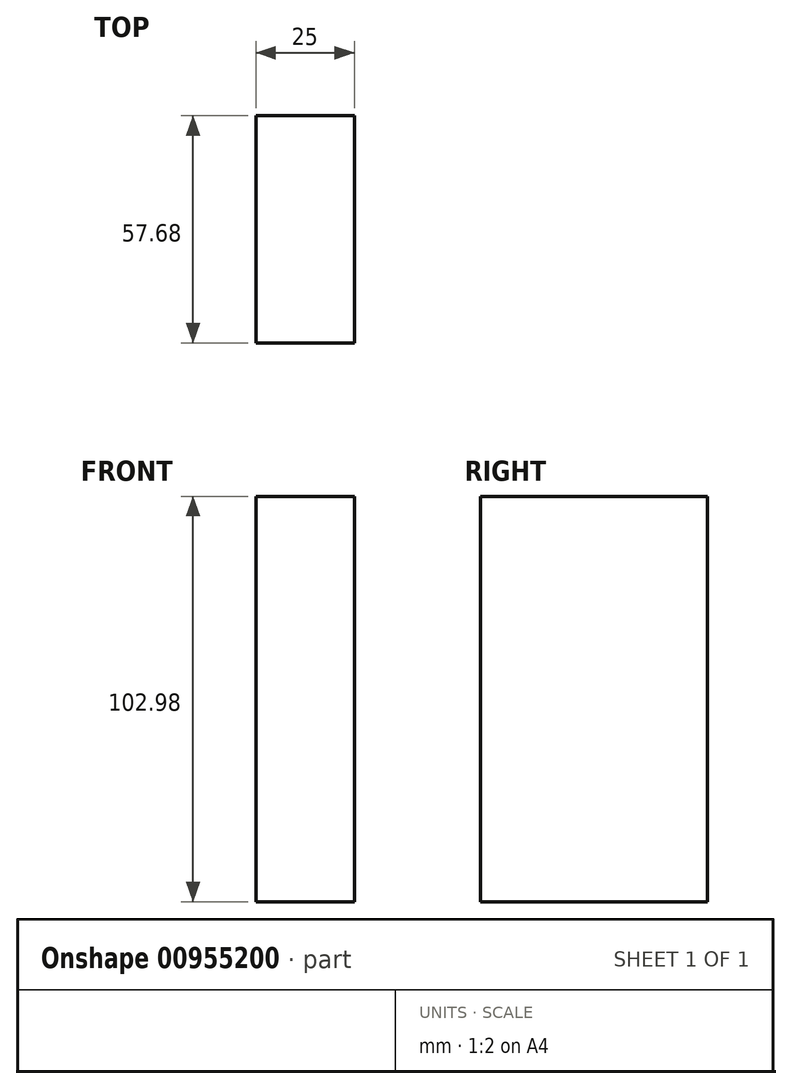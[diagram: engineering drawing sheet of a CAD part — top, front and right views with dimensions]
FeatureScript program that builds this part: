
annotation { "Feature Type Name" : "Feature", "Feature Type Description" : "" }
export const myFeature = defineFeature(function(context is Context, id is Id, definition is map)
    precondition{}
    {
        {
            var Q0;
            Q0=qCreatedBy(makeId("Right.planeOp"),FACE);
            var sketch = newSketch(context, id + "F0", { "sketchPlane" : qUnion([Q0])});
            skLineSegment(sketch, "E0.bottom", {"start": v(39.63, -62.92) * mm, "end": v(-18.05, -62.92) * mm});
            skLineSegment(sketch, "E0.top", {"start": v(39.63, 40.06) * mm, "end": v(-18.05, 40.06) * mm});
            skLineSegment(sketch, "E0.left", {"start": v(39.63, -62.92) * mm, "end": v(39.63, 40.06) * mm});
            skLineSegment(sketch, "E0.right", {"start": v(-18.05, -62.92) * mm, "end": v(-18.05, 40.06) * mm});
            skSolve(sketch);
        }
        {
            var Q0;
            Q0 = qSketchRegion(id + "F0", true);
            extrude(context, id + "F1", {"entities" : qUnion([Q0]), "depth" : 25 * mm, "offsetDistance" : 25 * mm});
        }
    });
